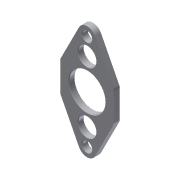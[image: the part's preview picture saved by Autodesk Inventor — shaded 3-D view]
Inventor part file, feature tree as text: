
AUTODESK INVENTOR PART (.ipt)
format: ipt  version: 2013 (Build 170138000, 138)  size: 117,760 bytes
history: native  units: in
note: dims shown in document units (in); Inventor stores cm internally (conversion verified against a paired STEP export)
features: chamfer x1, other x1, imported_body x1
ambient origin geometry x8: Origin, YZ Plane, XZ Plane, XY Plane, X Axis, Y Axis, Z Axis, Center Point
feature tree (3):
  chamfer  "Chamfer1"  [1 undecoded]
  other  "CIM Spacer 1251"
  imported_body  "Base1"
note: 1 required parameter value undecoded (feature->parameter linkage not recoverable at this tier; creation-order binding heuristic only, values carry confidence <= 0.55)
